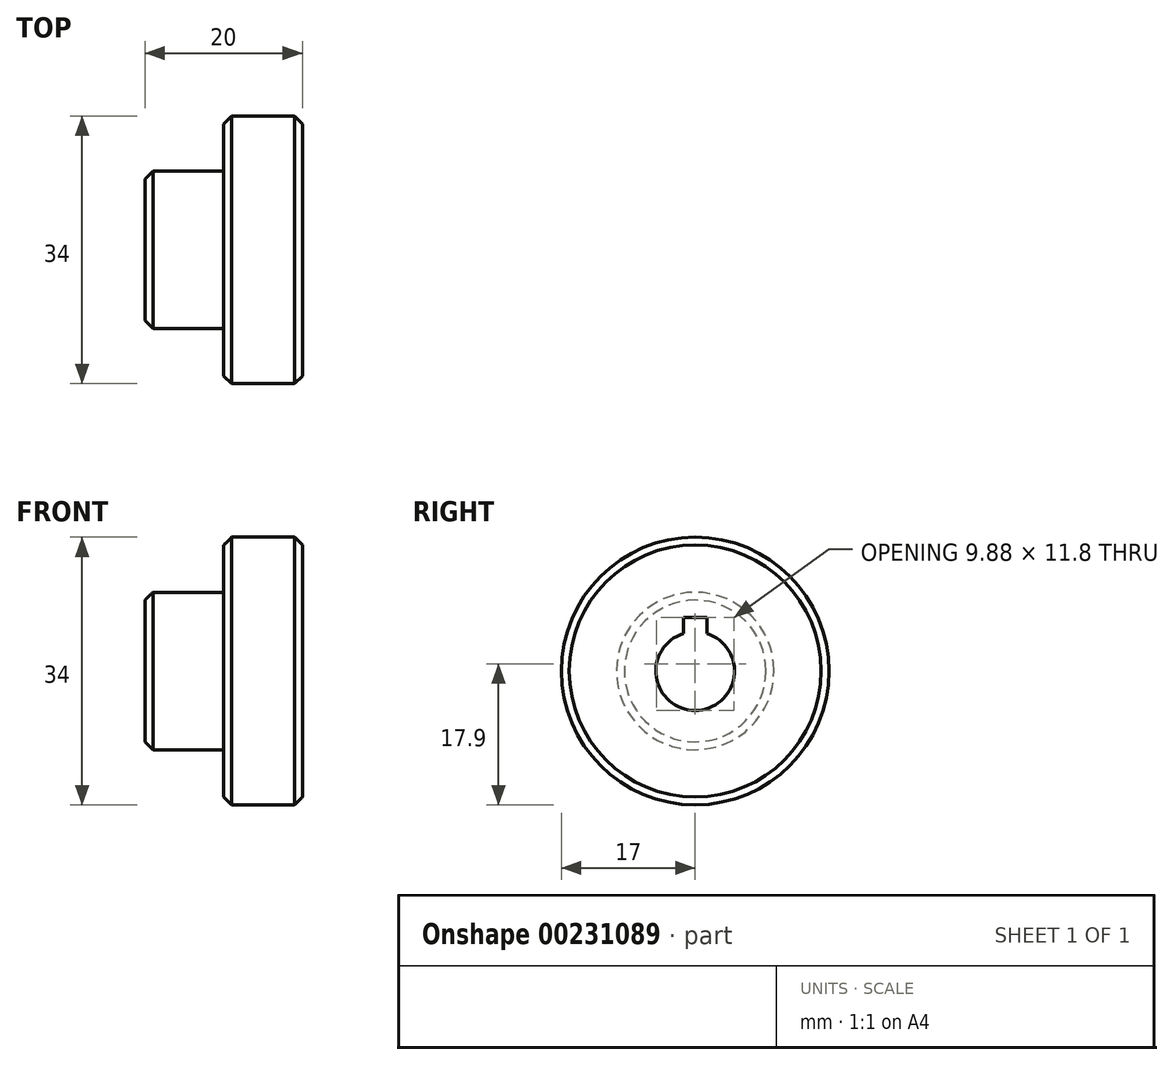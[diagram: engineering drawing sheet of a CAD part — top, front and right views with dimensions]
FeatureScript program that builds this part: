
annotation { "Feature Type Name" : "Feature", "Feature Type Description" : "" }
export const myFeature = defineFeature(function(context is Context, id is Id, definition is map)
    precondition{}
    {
        {
            var Q0;
            Q0=qCreatedBy(makeId("Front.planeOp"),FACE);
            var sketch = newSketch(context, id + "F0", { "sketchPlane" : qUnion([Q0])});
            skLineSegment(sketch, "E0", {"start": v(0, 0) * mm, "end": v(0, 10) * mm});
            skLineSegment(sketch, "E1", {"start": v(0, 10) * mm, "end": v(10, 10) * mm});
            skLineSegment(sketch, "E2", {"start": v(10, 10) * mm, "end": v(10, 17) * mm});
            skLineSegment(sketch, "E3", {"start": v(10, 17) * mm, "end": v(20, 17) * mm});
            skLineSegment(sketch, "E4", {"start": v(20, 17) * mm, "end": v(20, 0) * mm});
            skLineSegment(sketch, "E5", {"start": v(0, 0) * mm, "end": v(20, 0) * mm, "construction": true});
            skLineSegment(sketch, "E6", {"start": v(0, 0) * mm, "end": v(20, 0) * mm});
            skSolve(sketch);
        }
        {
            var Q0;
            Q0 = qSketchRegion(id + "F0", true);
            var Q1;
            Q1=sQuery(id+"F0.wireOp",EDGE,"E5");
            revolve(context, id + "F1", {"entities" : qUnion([Q0]), "axis" : qUnion([Q1]), "revolveType" : RevolveType.FULL});
        }
        {
            var Q0;
            Q0=makeQuery(id+"F1.opRevolve","SWEPT_EDGE",EDGE,{"disambiguationData":[OSD([sQuery(id+"F0.wireOp",EDGE,"E2"),sQuery(id+"F0.wireOp",EDGE,"E3")])]});
            var Q1;
            Q1=makeQuery(id+"F1.opRevolve","SWEPT_EDGE",EDGE,{"disambiguationData":[OSD([sQuery(id+"F0.wireOp",EDGE,"E0"),sQuery(id+"F0.wireOp",EDGE,"E1")])]});
            var Q2;
            Q2=makeQuery(id+"F1.opRevolve","SWEPT_EDGE",EDGE,{"disambiguationData":[OSD([sQuery(id+"F0.wireOp",EDGE,"E3"),sQuery(id+"F0.wireOp",EDGE,"E4")])]});
            chamfer(context, id + "F2", {"entities" : qUnion([Q0, Q1, Q2]), "width" : 1 * mm, "tangentPropagation" : true});
        }
        {
            var Q0;
            Q0=makeQuery(id+"F1.opRevolve","SWEPT_FACE",FACE,{"disambiguationData":[OSD([sQuery(id+"F0.wireOp",EDGE,"E4")])]});
            var sketch = newSketch(context, id + "F3", { "sketchPlane" : qUnion([Q0])});
            skArc(sketch, "E7", {"start": v(-1.5, 4.77) * mm, "mid": v(0, -5) * mm, "end": v(1.5, 4.77) * mm});
            skLineSegment(sketch, "E8", {"start": v(0, 6.8) * mm, "end": v(1.5, 6.8) * mm});
            skLineSegment(sketch, "E9", {"start": v(1.5, 6.8) * mm, "end": v(1.5, 4.77) * mm});
            skLineSegment(sketch, "E10.MirrorCS", {"start": v(0, 6.8) * mm, "end": v(-1.5, 6.8) * mm});
            skLineSegment(sketch, "E11.MirrorCS", {"start": v(-1.5, 6.8) * mm, "end": v(-1.5, 4.77) * mm});
            skSolve(sketch);
        }
        {
            var Q0;
            Q0 = qSketchRegion(id + "F3", true);
            extrude(context, id + "F4", {"entities" : qUnion([Q0]), "operationType" : NewBodyOperationType.REMOVE, "oppositeDirection" : true, "depth" : 20 * mm});
        }
    });
